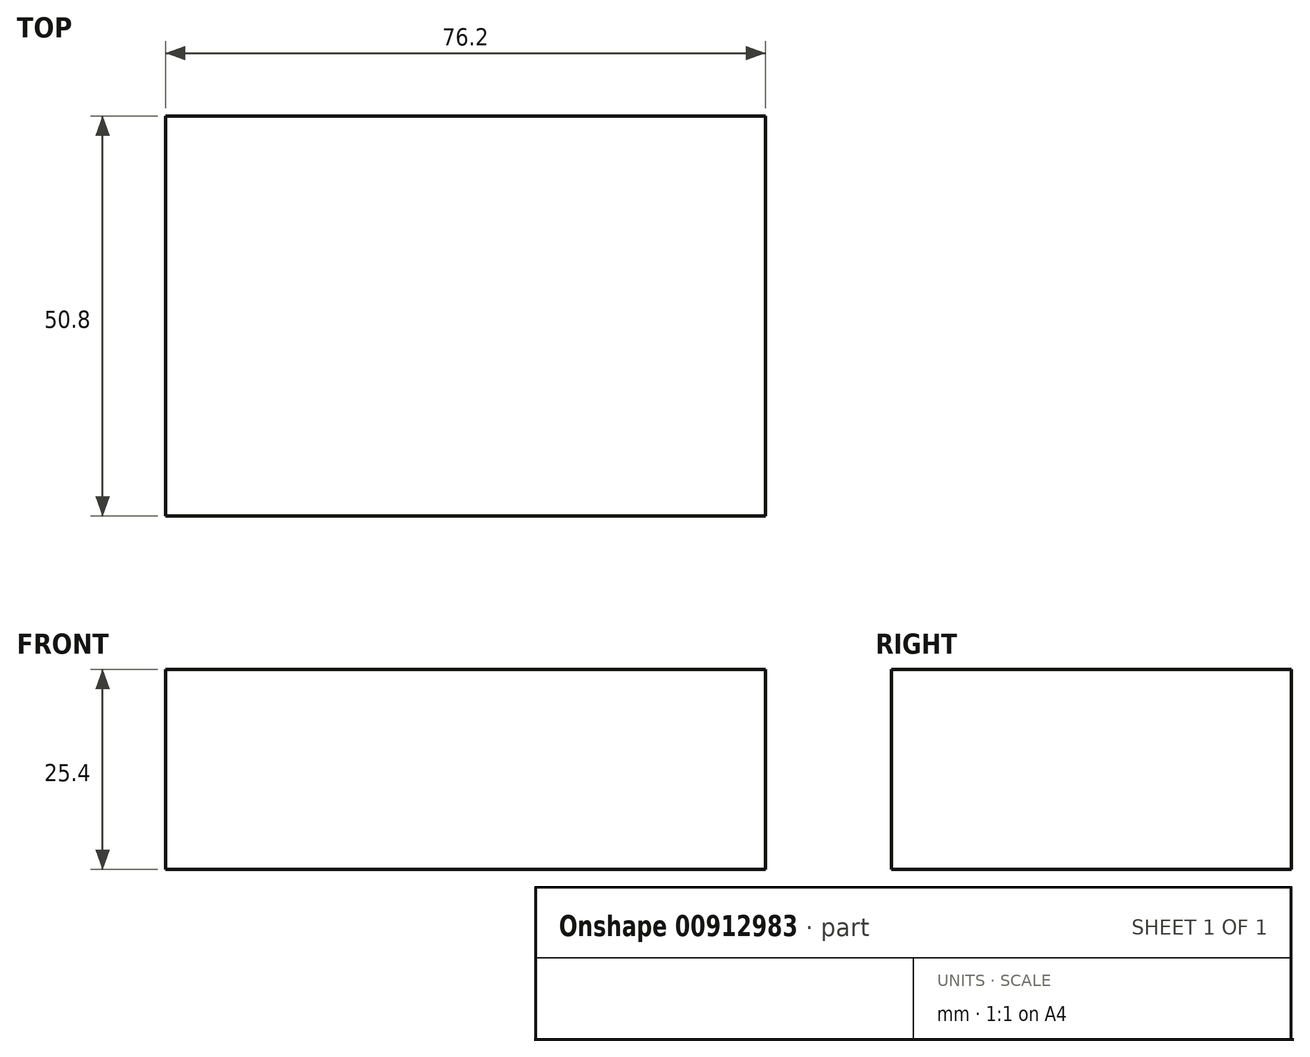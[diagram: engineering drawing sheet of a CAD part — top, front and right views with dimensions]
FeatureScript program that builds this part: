
annotation { "Feature Type Name" : "Feature", "Feature Type Description" : "" }
export const myFeature = defineFeature(function(context is Context, id is Id, definition is map)
    precondition{}
    {
        {
            var Q0;
            Q0=qCreatedBy(makeId("Top.planeOp"),FACE);
            var sketch = newSketch(context, id + "F0", { "sketchPlane" : qUnion([Q0])});
            skLineSegment(sketch, "E0.bottom", {"start": v(38.1, 25.4) * mm, "end": v(-38.1, 25.4) * mm});
            skLineSegment(sketch, "E0.top", {"start": v(38.1, -25.4) * mm, "end": v(-38.1, -25.4) * mm});
            skLineSegment(sketch, "E0.left", {"start": v(38.1, 25.4) * mm, "end": v(38.1, -25.4) * mm});
            skLineSegment(sketch, "E0.right", {"start": v(-38.1, 25.4) * mm, "end": v(-38.1, -25.4) * mm});
            skPoint(sketch, "E0.middle", {"position": v(0, 0) * mm});
            skSolve(sketch);
        }
        {
            var Q0;
            Q0=makeQuery(id+"F0.imprint","IMPRINT",FACE,{"disambiguationData":[TD([[makeQuery(id+"F0.imprint","IMPRINT",EDGE,{"derivedFrom":sQuery(id+"F0.wireOp",EDGE,"E0.bottom")}),1.0]])]});
            extrude(context, id + "F1", {"entities" : qUnion([Q0]), "depth" : 25.4 * mm, "offsetDistance" : 25.4 * mm});
        }
    });
